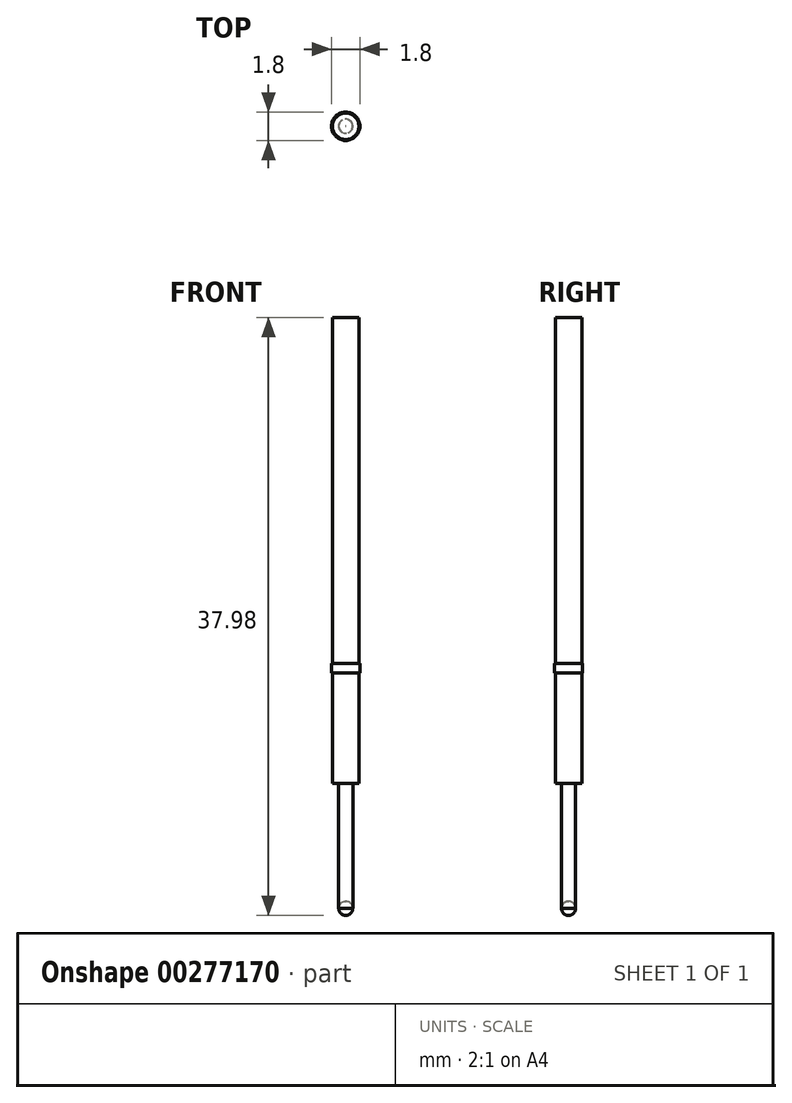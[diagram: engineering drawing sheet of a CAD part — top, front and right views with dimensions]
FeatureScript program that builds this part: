
annotation { "Feature Type Name" : "Feature", "Feature Type Description" : "" }
export const myFeature = defineFeature(function(context is Context, id is Id, definition is map)
    precondition{}
    {
        {
            var Q0;
            Q0=qCreatedBy(makeId("Top.planeOp"),FACE);
            var sketch = newSketch(context, id + "F0", { "sketchPlane" : qUnion([Q0])});
            skCircle(sketch, "E0", {"center": v(0, 0) * mm, "radius": 0.84 * mm});
            skSolve(sketch);
        }
        {
            var Q0;
            Q0=makeQuery(id+"F0.imprint","IMPRINT",FACE,{"disambiguationData":[TD([[makeQuery(id+"F0.imprint","IMPRINT",EDGE,{"derivedFrom":sQuery(id+"F0.wireOp",EDGE,"E0")}),1.0]])]});
            extrude(context, id + "F1", {"entities" : qUnion([Q0]), "depth" : 29.6 * mm});
        }
        {
            var Q0;
            Q0=qCreatedBy(makeId("Right.planeOp"),FACE);
            var sketch = newSketch(context, id + "F2", { "sketchPlane" : qUnion([Q0])});
            skLineSegment(sketch, "E1.bottom", {"start": v(0, 7.02) * mm, "end": v(0.9, 7.02) * mm});
            skLineSegment(sketch, "E1.top", {"start": v(0, 7.62) * mm, "end": v(0.9, 7.62) * mm});
            skLineSegment(sketch, "E1.left", {"start": v(0, 7.02) * mm, "end": v(0, 7.62) * mm});
            skLineSegment(sketch, "E1.right", {"start": v(0.9, 7.02) * mm, "end": v(0.9, 7.62) * mm});
            skSolve(sketch);
        }
        {
            var Q0;
            Q0=makeQuery(id+"F2.imprint","IMPRINT",FACE,{"disambiguationData":[TD([[makeQuery(id+"F2.imprint","IMPRINT",EDGE,{"derivedFrom":sQuery(id+"F2.wireOp",EDGE,"E1.bottom")}),1.0]])]});
            var Q1;
            Q1=sQuery(id+"F2.wireOp",EDGE,"E1.left");
            revolve(context, id + "F3", {"operationType" : NewBodyOperationType.ADD, "entities" : qUnion([Q0]), "axis" : qUnion([Q1]), "revolveType" : RevolveType.FULL});
        }
        {
            var Q0;
            Q0=qCreatedBy(makeId("Top.planeOp"),FACE);
            var sketch = newSketch(context, id + "F4", { "sketchPlane" : qUnion([Q0])});
            skCircle(sketch, "E2", {"center": v(0, 0) * mm, "radius": 0.46 * mm});
            skSolve(sketch);
        }
        {
            var Q0;
            Q0 = qSketchRegion(id + "F4", true);
            extrude(context, id + "F5", {"entities" : qUnion([Q0]), "operationType" : NewBodyOperationType.ADD, "oppositeDirection" : true, "depth" : 8.38 * mm});
        }
        {
            var Q0;
            Q0=makeQuery(id+"F5.opExtrude","CAP_EDGE",EDGE,{"disambiguationData":[OSD([sQuery(id+"F4.wireOp",EDGE,"E2")])],"isStart":false});
            fillet(context, id + "F6", {"entities" : qUnion([Q0]), "radius" : .45 * mm, "tangentPropagation" : true, "allowEdgeOverflow" : false});
        }
    });
